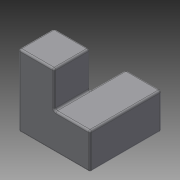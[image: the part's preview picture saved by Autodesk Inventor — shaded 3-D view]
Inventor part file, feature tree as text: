
AUTODESK INVENTOR PART (.ipt)
format: ipt  version: 2014 (Build 180170000, 170)  size: 185,856 bytes
history: native  units: in
note: dims shown in document units (in); Inventor stores cm internally (conversion verified against a paired STEP export)
features: plane x8, extrude x3, other x1, shell x1, fillet x1, sketch x1
ambient origin geometry x8: Origin, YZ Plane, XZ Plane, XY Plane, X Axis, Y Axis, Z Axis, Center Point
bodies: Solid1 (feature_tree)
feature tree (15):
  other  "Cube Master.ipt"
  extrude  "Extrusion1"  Depth=0.3937in
  extrude  "Extrusion2"  Depth=0.0193in TaperAngle=0.0deg
  extrude  "Extrusion3"  TaperAngle=0.0deg  [1 undecoded]
  shell  "Shell1"  Thickness=1.0in
  fillet  "Fillet1"  Radius=0.0394in
  sketch  "Sketch1"  dims[d0=0.3937in d1=0.3937in d2=1.0in d3=0.0in d4=0.0in d5=0.0in d6=1.0in d7=0.0in d8=0.0394in d9=0.0193in d10=0.0193in]
  plane  "Work Plane1"
  plane  "Work Plane2"
  plane  "Work Plane3"
  plane  "Work Plane4"
  plane  "Work Plane5"
  plane  "Work Plane6"
  plane  "Work Plane7"
  plane  "Work Plane8"
note: 1 required parameter value undecoded (feature->parameter linkage not recoverable at this tier; creation-order binding heuristic only, values carry confidence <= 0.55)
